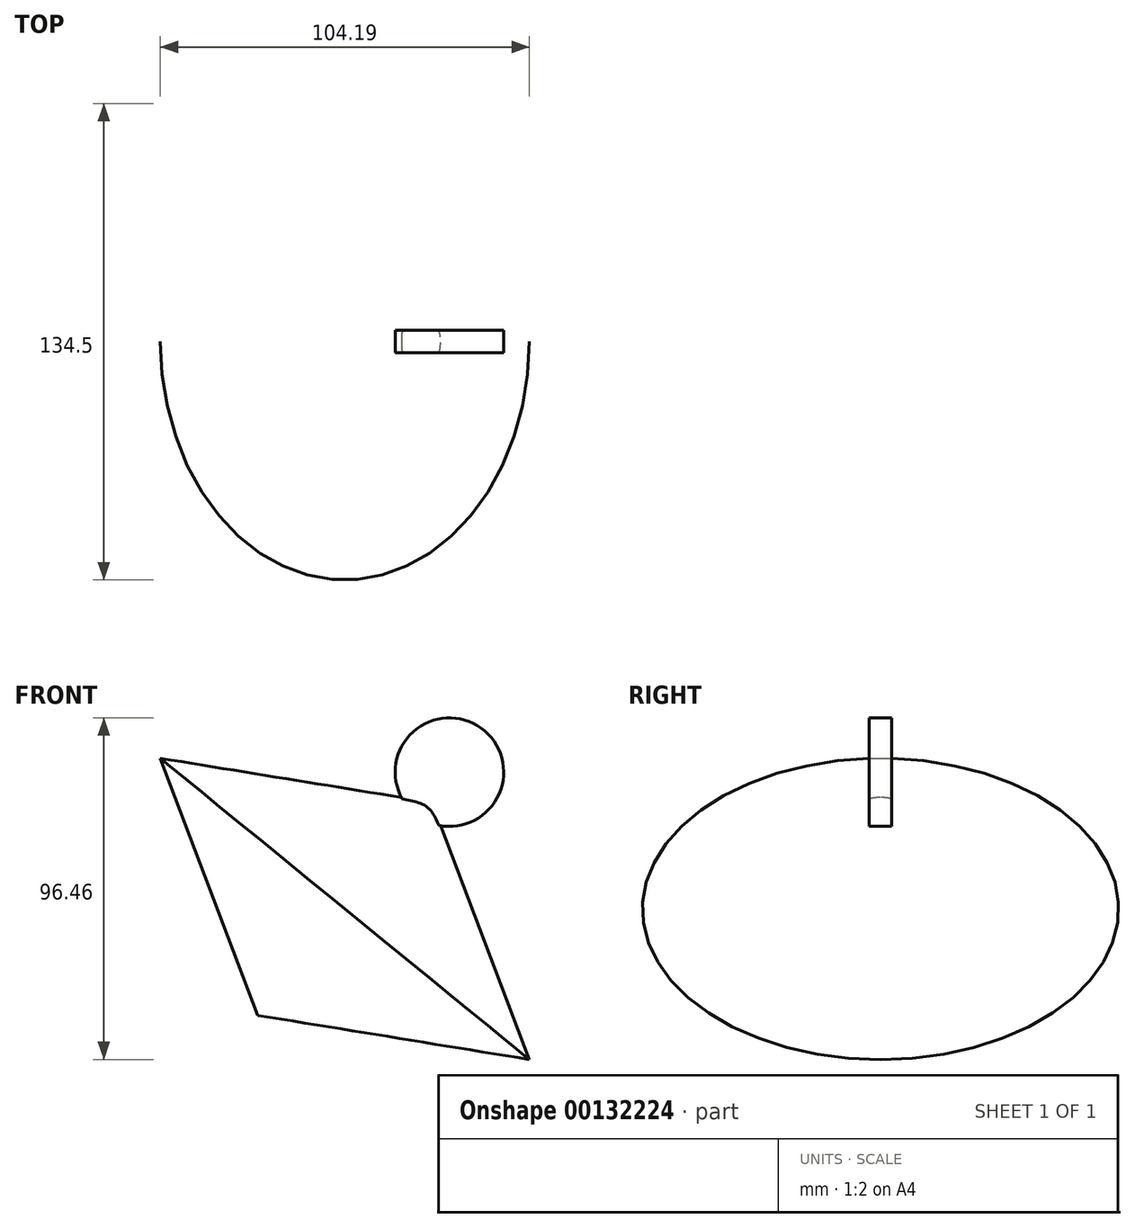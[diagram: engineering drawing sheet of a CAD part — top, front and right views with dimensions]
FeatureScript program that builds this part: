
annotation { "Feature Type Name" : "Feature", "Feature Type Description" : "" }
export const myFeature = defineFeature(function(context is Context, id is Id, definition is map)
    precondition{}
    {
        {
            var Q0;
            Q0=qCreatedBy(makeId("Front.planeOp"),FACE);
            var sketch = newSketch(context, id + "F0", { "sketchPlane" : qUnion([Q0])});
            skCircle(sketch, "E0.cCircle", {"center": v(0, 0) * mm, "radius": 22.42 * mm, "construction": true});
            skLineSegment(sketch, "E0.0", {"start": v(-41.92, -15.9) * mm, "end": v(7.19, 44.25) * mm});
            skLineSegment(sketch, "E0.1", {"start": v(7.19, 44.25) * mm, "end": v(34.73, -28.35) * mm});
            skLineSegment(sketch, "E0.2", {"start": v(34.73, -28.35) * mm, "end": v(-41.92, -15.9) * mm});
            skPoint(sketch, "E0.0.midPoint", {"position": v(-17.37, 14.18) * mm});
            skSolve(sketch);
        }
        {
            var Q0;
            Q0=makeQuery(id+"F0.imprint","IMPRINT",FACE,{"disambiguationData":[TD([[makeQuery(id+"F0.imprint","IMPRINT",EDGE,{"derivedFrom":sQuery(id+"F0.wireOp",EDGE,"E0.0")}),-1.0]])]});
            var Q1;
            Q1=sQuery(id+"F0.wireOp",EDGE,"E0.0");
            revolve(context, id + "F1", {"entities" : qUnion([Q0]), "axis" : qUnion([Q1]), "revolveType" : RevolveType.FULL});
        }
        {
            var Q0;
            Q0=qCreatedBy(makeId("Front.planeOp"),FACE);
            var sketch = newSketch(context, id + "F2", { "sketchPlane" : qUnion([Q0])});
            skCircle(sketch, "E1", {"center": v(12.18, 52.79) * mm, "radius": 15.33 * mm});
            skSolve(sketch);
        }
        {
            var Q0;
            Q0=makeQuery(id+"F2.imprint","IMPRINT",FACE,{"disambiguationData":[TD([[makeQuery(id+"F2.imprint","IMPRINT",EDGE,{"derivedFrom":sQuery(id+"F2.wireOp",EDGE,"E1")}),1.0]])]});
            extrude(context, id + "F3", {"entities" : qUnion([Q0]), "operationType" : NewBodyOperationType.ADD, "endBound" : BoundingType.SYMMETRIC, "depth" : 6.35 * mm});
        }
    });
